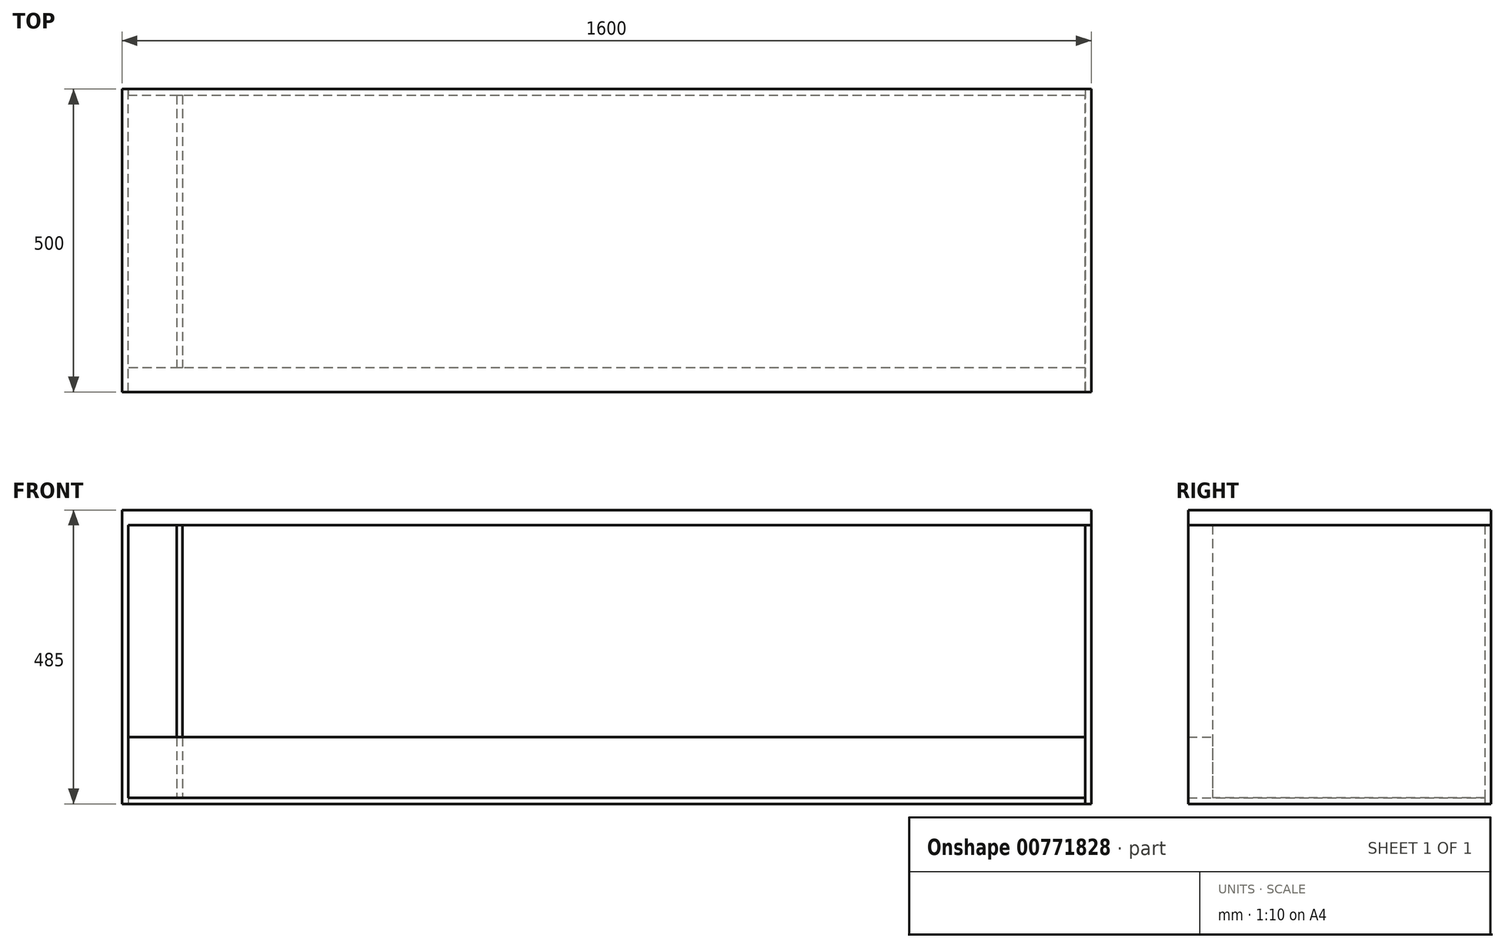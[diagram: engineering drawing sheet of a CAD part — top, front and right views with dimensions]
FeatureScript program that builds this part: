
annotation { "Feature Type Name" : "Feature", "Feature Type Description" : "" }
export const myFeature = defineFeature(function(context is Context, id is Id, definition is map)
    precondition{}
    {
        {
            var Q0;
            Q0=qCreatedBy(makeId("Top.planeOp"),FACE);
            var sketch = newSketch(context, id + "F0", { "sketchPlane" : qUnion([Q0])});
            skLineSegment(sketch, "E0.bottom", {"start": v(0, 0) * mm, "end": v(1600, 0) * mm});
            skLineSegment(sketch, "E0.top", {"start": v(0, 500) * mm, "end": v(1600, 500) * mm});
            skLineSegment(sketch, "E0.left", {"start": v(0, 0) * mm, "end": v(0, 500) * mm});
            skLineSegment(sketch, "E0.right", {"start": v(1600, 0) * mm, "end": v(1600, 500) * mm});
            skSolve(sketch);
        }
        {
            var Q0;
            Q0=makeQuery(id+"F0.imprint","IMPRINT",FACE,{"disambiguationData":[TD([[makeQuery(id+"F0.imprint","IMPRINT",EDGE,{"derivedFrom":sQuery(id+"F0.wireOp",EDGE,"E0.bottom")}),1.0]])]});
            extrude(context, id + "F1", {"entities" : qUnion([Q0]), "depth" : 25 * mm, "offsetDistance" : 25 * mm});
        }
        {
            var Q0;
            Q0=makeQuery(id+"F0.imprint","IMPRINT",FACE,{"disambiguationData":[TD([[makeQuery(id+"F0.imprint","IMPRINT",EDGE,{"derivedFrom":sQuery(id+"F0.wireOp",EDGE,"E0.bottom")}),1.0]])]});
            cPlane(context, id + "F2", {"entities" : qUnion([Q0]), "cplaneType" : CPlaneType.OFFSET, "offset" : 460 * mm, "oppositeDirection" : true, "width" : 150 * mm, "height" : 150 * mm});
        }
        {
            var Q0;
            Q0=qCreatedBy(id+"F2.planeOp",FACE);
            var sketch = newSketch(context, id + "F3", { "sketchPlane" : qUnion([Q0])});
            skLineSegment(sketch, "E1.bottom", {"start": v(10, 0) * mm, "end": v(1590, 0) * mm});
            skLineSegment(sketch, "E1.top", {"start": v(10, 490) * mm, "end": v(1590, 490) * mm});
            skLineSegment(sketch, "E1.left", {"start": v(10, 0) * mm, "end": v(10, 490) * mm});
            skLineSegment(sketch, "E1.right", {"start": v(1590, 0) * mm, "end": v(1590, 490) * mm});
            skSolve(sketch);
        }
        {
            var Q0;
            Q0=makeQuery(id+"F3.imprint","IMPRINT",FACE,{"disambiguationData":[TD([[makeQuery(id+"F3.imprint","IMPRINT",EDGE,{"derivedFrom":sQuery(id+"F3.wireOp",EDGE,"E1.bottom")}),1.0]])]});
            extrude(context, id + "F4", {"entities" : qUnion([Q0]), "depth" : 10 * mm, "offsetDistance" : 25 * mm});
        }
        {
            var Q0;
            Q0=makeQuery(id+"F0.imprint","IMPRINT",FACE,{"disambiguationData":[TD([[makeQuery(id+"F0.imprint","IMPRINT",EDGE,{"derivedFrom":sQuery(id+"F0.wireOp",EDGE,"E0.bottom")}),1.0]])]});
            var sketch = newSketch(context, id + "F5", { "sketchPlane" : qUnion([Q0])});
            skLineSegment(sketch, "E2.bottom", {"start": v(0, 0) * mm, "end": v(10, 0) * mm});
            skLineSegment(sketch, "E2.top", {"start": v(0, 500) * mm, "end": v(10, 500) * mm});
            skLineSegment(sketch, "E2.left", {"start": v(0, 0) * mm, "end": v(0, 500) * mm});
            skLineSegment(sketch, "E2.right", {"start": v(10, 0) * mm, "end": v(10, 500) * mm});
            skSolve(sketch);
        }
        {
            var Q0;
            Q0=qSketchRegion(id+"F5",true);
            var Q1;
            Q1=makeQuery(id+"F4.opExtrude","CAP_FACE",FACE,{"disambiguationData":[OSD([sQuery(id+"F3.wireOp",EDGE,"E1.bottom"),sQuery(id+"F3.wireOp",EDGE,"E1.top"),sQuery(id+"F3.wireOp",EDGE,"E1.left"),sQuery(id+"F3.wireOp",EDGE,"E1.right")])],"isStart":true});
            extrude(context, id + "F6", {"entities" : qUnion([Q0]), "operationType" : NewBodyOperationType.ADD, "endBound" : BoundingType.UP_TO_SURFACE, "oppositeDirection" : true, "depth" : 25 * mm, "endBoundEntityFace" : qUnion([Q1]), "offsetDistance" : 25 * mm});
        }
        {
            var Q0;
            Q0=makeQuery(id+"F0.imprint","IMPRINT",FACE,{"disambiguationData":[TD([[makeQuery(id+"F0.imprint","IMPRINT",EDGE,{"derivedFrom":sQuery(id+"F0.wireOp",EDGE,"E0.bottom")}),1.0]])]});
            var sketch = newSketch(context, id + "F7", { "sketchPlane" : qUnion([Q0])});
            skLineSegment(sketch, "E3.bottom", {"start": v(1600, 0) * mm, "end": v(1590, 0) * mm});
            skLineSegment(sketch, "E3.top", {"start": v(1600, 500) * mm, "end": v(1590, 500) * mm});
            skLineSegment(sketch, "E3.left", {"start": v(1600, 0) * mm, "end": v(1600, 500) * mm});
            skLineSegment(sketch, "E3.right", {"start": v(1590, 0) * mm, "end": v(1590, 500) * mm});
            skSolve(sketch);
        }
        {
            var Q0;
            Q0=makeQuery(id+"F7.imprint","IMPRINT",FACE,{"disambiguationData":[TD([[makeQuery(id+"F7.imprint","IMPRINT",EDGE,{"derivedFrom":sQuery(id+"F7.wireOp",EDGE,"E3.bottom")}),1.0]])]});
            var Q1;
            Q1=makeQuery(id+"F4.opExtrude","CAP_FACE",FACE,{"disambiguationData":[OSD([sQuery(id+"F3.wireOp",EDGE,"E1.bottom"),sQuery(id+"F3.wireOp",EDGE,"E1.top"),sQuery(id+"F3.wireOp",EDGE,"E1.left"),sQuery(id+"F3.wireOp",EDGE,"E1.right")])],"isStart":true});
            extrude(context, id + "F8", {"entities" : qUnion([Q0]), "endBound" : BoundingType.UP_TO_SURFACE, "oppositeDirection" : true, "depth" : 25 * mm, "endBoundEntityFace" : qUnion([Q1]), "offsetDistance" : 25 * mm});
        }
        {
            var Q0;
            Q0=makeQuery(id+"F6.opExtrude","SWEPT_FACE",FACE,{"disambiguationData":[OSD([sQuery(id+"F5.wireOp",EDGE,"E2.right")])]});
            var sketch = newSketch(context, id + "F9", { "sketchPlane" : qUnion([Q0])});
            skLineSegment(sketch, "E4.bottom", {"start": v(0, -350) * mm, "end": v(40, -350) * mm});
            skLineSegment(sketch, "E4.top", {"start": v(0, -450) * mm, "end": v(40, -450) * mm});
            skLineSegment(sketch, "E4.left", {"start": v(0, -350) * mm, "end": v(0, -450) * mm});
            skLineSegment(sketch, "E4.right", {"start": v(40, -350) * mm, "end": v(40, -450) * mm});
            skSolve(sketch);
        }
        {
            var Q0;
            Q0=makeQuery(id+"F9.imprint","IMPRINT",FACE,{"disambiguationData":[TD([[makeQuery(id+"F9.imprint","IMPRINT",EDGE,{"derivedFrom":sQuery(id+"F9.wireOp",EDGE,"E4.bottom")}),-1.0]])]});
            extrude(context, id + "F10", {"entities" : qUnion([Q0]), "endBound" : BoundingType.UP_TO_NEXT, "depth" : 25 * mm, "offsetDistance" : 25 * mm});
        }
        {
            var Q0;
            Q0=makeQuery(id+"F4.opExtrude","CAP_FACE",FACE,{"disambiguationData":[OSD([sQuery(id+"F3.wireOp",EDGE,"E1.bottom"),sQuery(id+"F3.wireOp",EDGE,"E1.top"),sQuery(id+"F3.wireOp",EDGE,"E1.left"),sQuery(id+"F3.wireOp",EDGE,"E1.right")])],"isStart":false});
            var sketch = newSketch(context, id + "F11", { "sketchPlane" : qUnion([Q0])});
            skLineSegment(sketch, "E5.bottom", {"start": v(100, 490) * mm, "end": v(90, 490) * mm});
            skLineSegment(sketch, "E5.top", {"start": v(100, 40) * mm, "end": v(90, 40) * mm});
            skLineSegment(sketch, "E5.left", {"start": v(100, 490) * mm, "end": v(100, 40) * mm});
            skLineSegment(sketch, "E5.right", {"start": v(90, 490) * mm, "end": v(90, 40) * mm});
            skSolve(sketch);
        }
        {
            var Q0;
            Q0=makeQuery(id+"F11.imprint","IMPRINT",FACE,{"disambiguationData":[TD([[makeQuery(id+"F11.imprint","IMPRINT",EDGE,{"derivedFrom":sQuery(id+"F11.wireOp",EDGE,"E5.bottom")}),-1.0]])]});
            extrude(context, id + "F12", {"entities" : qUnion([Q0]), "endBound" : BoundingType.UP_TO_NEXT, "depth" : 25 * mm, "offsetDistance" : 25 * mm});
        }
    });
